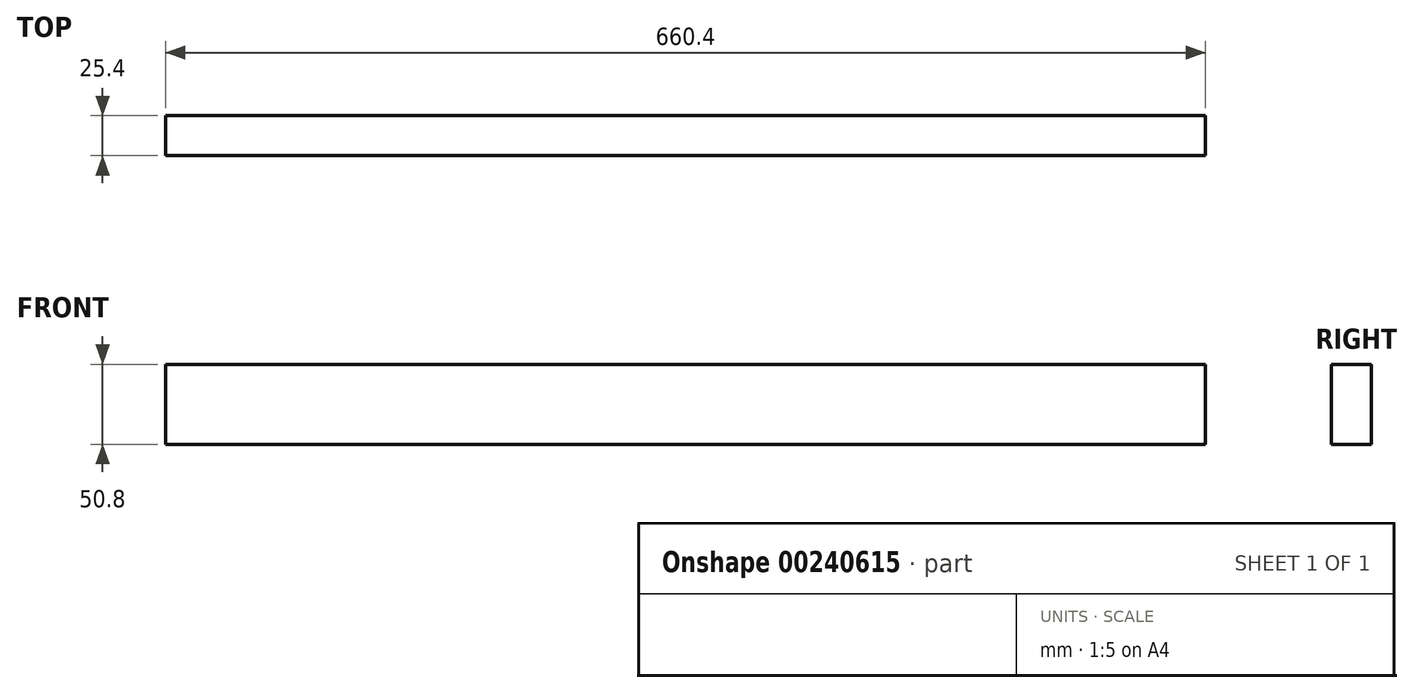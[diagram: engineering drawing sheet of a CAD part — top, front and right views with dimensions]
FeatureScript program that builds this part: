
annotation { "Feature Type Name" : "Feature", "Feature Type Description" : "" }
export const myFeature = defineFeature(function(context is Context, id is Id, definition is map)
    precondition{}
    {
        {
            var Q0;
            Q0=qCreatedBy(makeId("Right.planeOp"),FACE);
            var sketch = newSketch(context, id + "F0", { "sketchPlane" : qUnion([Q0])});
            skLineSegment(sketch, "E0.bottom", {"start": v(-12.7, 25.4) * mm, "end": v(12.7, 25.4) * mm});
            skLineSegment(sketch, "E0.top", {"start": v(-12.7, -25.4) * mm, "end": v(12.7, -25.4) * mm});
            skLineSegment(sketch, "E0.left", {"start": v(-12.7, 25.4) * mm, "end": v(-12.7, -25.4) * mm});
            skLineSegment(sketch, "E0.right", {"start": v(12.7, 25.4) * mm, "end": v(12.7, -25.4) * mm});
            skSolve(sketch);
        }
        {
            var Q0;
            Q0=makeQuery(id+"F0.imprint","IMPRINT",FACE,{"disambiguationData":[TD([[makeQuery(id+"F0.imprint","IMPRINT",EDGE,{"derivedFrom":sQuery(id+"F0.wireOp",EDGE,"E0.bottom")}),-1.0]])]});
            extrude(context, id + "F1", {"entities" : qUnion([Q0]), "endBound" : BoundingType.SYMMETRIC, "depth" : 660.4 * mm, "offsetDistance" : 25.4 * mm});
        }
    });
